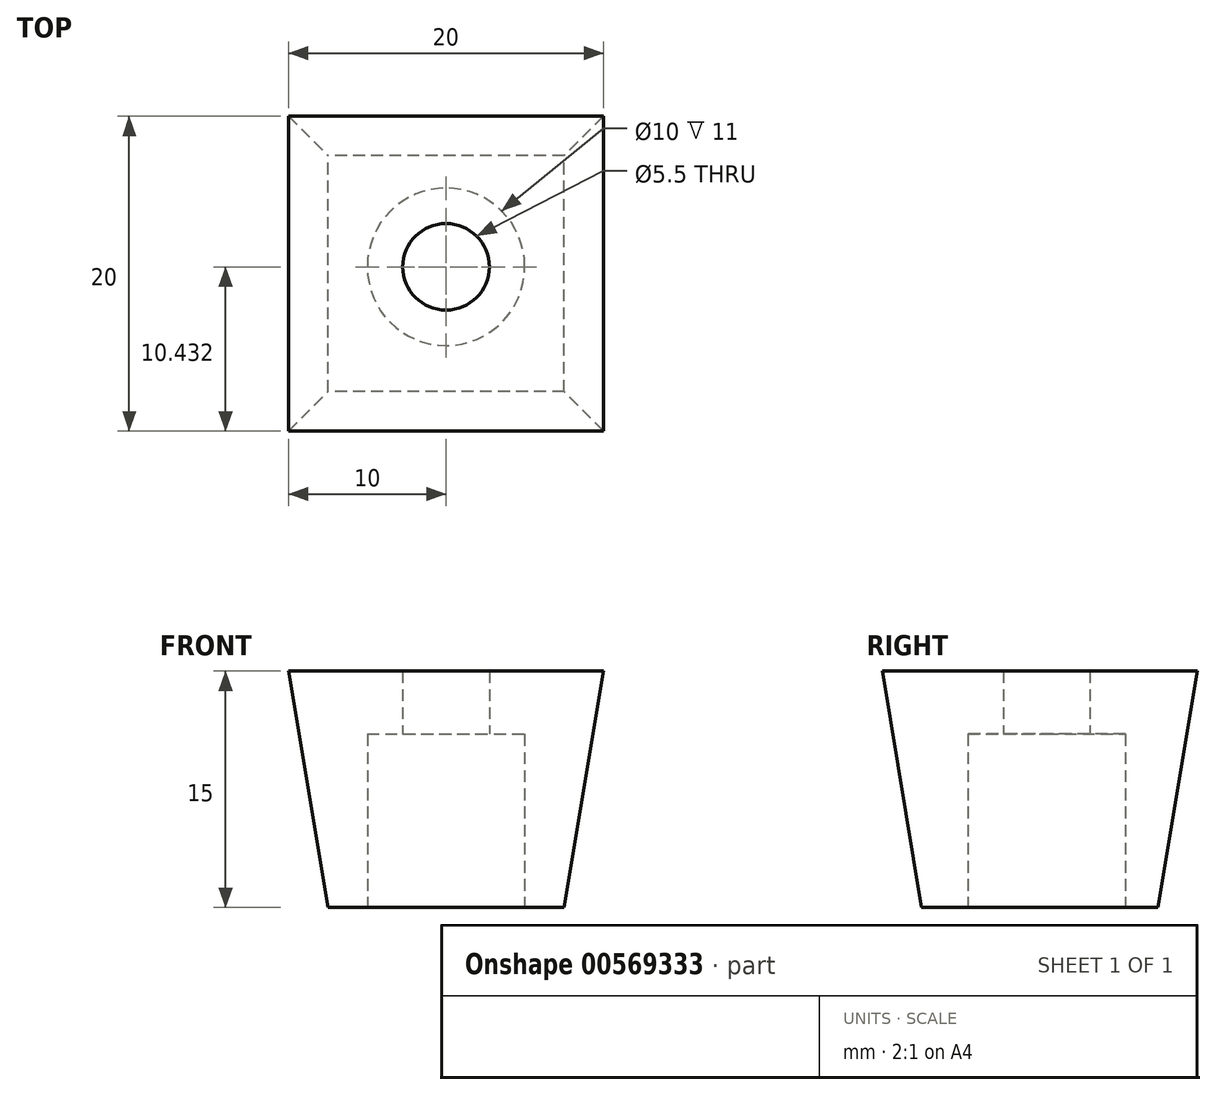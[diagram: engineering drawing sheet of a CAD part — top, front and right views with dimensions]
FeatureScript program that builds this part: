
annotation { "Feature Type Name" : "Feature", "Feature Type Description" : "" }
export const myFeature = defineFeature(function(context is Context, id is Id, definition is map)
    precondition{}
    {
        {
            var Q0;
            Q0=qCreatedBy(makeId("Top.planeOp"),FACE);
            var sketch = newSketch(context, id + "F0", { "sketchPlane" : qUnion([Q0])});
            skLineSegment(sketch, "E0.bottom", {"start": v(10, 10) * mm, "end": v(-10, 10) * mm});
            skLineSegment(sketch, "E0.top", {"start": v(10, -10) * mm, "end": v(-10, -10) * mm});
            skLineSegment(sketch, "E0.left", {"start": v(10, 10) * mm, "end": v(10, -10) * mm});
            skLineSegment(sketch, "E0.right", {"start": v(-10, 10) * mm, "end": v(-10, -10) * mm});
            skPoint(sketch, "E0.middle", {"position": v(0, 0) * mm});
            skSolve(sketch);
        }
        {
            var Q0;
            Q0=qCreatedBy(makeId("Top.planeOp"),FACE);
            cPlane(context, id + "F1", {"entities" : qUnion([Q0]), "cplaneType" : CPlaneType.OFFSET, "offset" : 15 * mm, "oppositeDirection" : true, "width" : 150 * mm, "height" : 150 * mm});
        }
        {
            var Q0;
            Q0=qCreatedBy(id+"F1.planeOp",FACE);
            var sketch = newSketch(context, id + "F2", { "sketchPlane" : qUnion([Q0])});
            skLineSegment(sketch, "E1.bottom", {"start": v(7.5, -7.5) * mm, "end": v(-7.5, -7.5) * mm});
            skLineSegment(sketch, "E1.top", {"start": v(7.5, 7.5) * mm, "end": v(-7.5, 7.5) * mm});
            skLineSegment(sketch, "E1.left", {"start": v(7.5, -7.5) * mm, "end": v(7.5, 7.5) * mm});
            skLineSegment(sketch, "E1.right", {"start": v(-7.5, -7.5) * mm, "end": v(-7.5, 7.5) * mm});
            skPoint(sketch, "E1.middle", {"position": v(0, 0) * mm});
            skSolve(sketch);
        }
        {
            var Q0;
            Q0=makeQuery(id+"F0.imprint","IMPRINT",FACE,{"disambiguationData":[TD([[makeQuery(id+"F0.imprint","IMPRINT",EDGE,{"derivedFrom":sQuery(id+"F0.wireOp",EDGE,"E0.bottom")}),1.0]])]});
            var Q1;
            Q1=makeQuery(id+"F2.imprint","IMPRINT",FACE,{"disambiguationData":[TD([[makeQuery(id+"F2.imprint","IMPRINT",EDGE,{"derivedFrom":sQuery(id+"F2.wireOp",EDGE,"E1.bottom")}),-1.0]])]});
            loft(context, id + "F3", {"sheetProfilesArray" : [{ "sheetProfileEntities" : qUnion([Q0]) }, { "sheetProfileEntities" : qUnion([Q1]) }]});
        }
        {
            var Q0;
            Q0=makeQuery(id+"F3.opLoft","CAP_FACE",FACE,{"disambiguationData":[OSD([makeQuery(id+"F2.imprint","IMPRINT",FACE,{"disambiguationData":[TD([[makeQuery(id+"F2.imprint","IMPRINT",EDGE,{"derivedFrom":sQuery(id+"F2.wireOp",EDGE,"E1.bottom")}),-1.0]])]})])],"isStart":true});
            var sketch = newSketch(context, id + "F4", { "sketchPlane" : qUnion([Q0])});
            skCircle(sketch, "E2", {"center": v(0, -0.43) * mm, "radius": 5 * mm});
            skSolve(sketch);
        }
        {
            var Q0;
            Q0 = qSketchRegion(id + "F4", true);
            extrude(context, id + "F5", {"entities" : qUnion([Q0]), "operationType" : NewBodyOperationType.REMOVE, "oppositeDirection" : true, "depth" : 11 * mm, "offsetDistance" : 25 * mm});
        }
        {
            var Q0;
            Q0=makeQuery(id+"F5.boolean.opBoolean","COPY",FACE,{"derivedFrom":makeQuery(id+"F5.opExtrude","CAP_FACE",FACE,{"disambiguationData":[OSD([sQuery(id+"F4.wireOp",EDGE,"E2")])],"isStart":false})});
            var sketch = newSketch(context, id + "F6", { "sketchPlane" : qUnion([Q0])});
            skCircle(sketch, "E3", {"center": v(0, -0.43) * mm, "radius": 2.75 * mm});
            skSolve(sketch);
        }
        {
            var Q0;
            Q0 = qSketchRegion(id + "F6", true);
            extrude(context, id + "F7", {"entities" : qUnion([Q0]), "operationType" : NewBodyOperationType.REMOVE, "oppositeDirection" : true, "depth" : 10 * mm, "offsetDistance" : 25 * mm});
        }
    });
